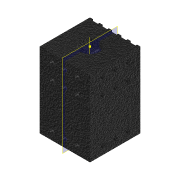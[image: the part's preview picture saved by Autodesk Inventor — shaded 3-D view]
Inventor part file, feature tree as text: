
AUTODESK INVENTOR PART (.ipt)
format: ipt  version: 2022 (Build 260153000, 153)  size: 360,448 bytes
history: native  units: mm
features: sketch x6, extrude x5, projected_geometry x3, plane x2, other x1, pattern_circular x1, pattern_linear x1, reference x1
ambient origin geometry x8: Origin, YZ Plane, XZ Plane, XY Plane, X Axis, Y Axis, Z Axis, Center Point
bodies: Volumenkörper1 (feature_tree)
feature tree (20):
  extrude  "Extrusion1"  Depth=32.0mm
  extrude  "Extrusion2"  Depth=5.0mm
  extrude  "Extrusion3"  Depth=2.8mm
  extrude  "Extrusion4"  Depth=8.0mm
  other  "Arbeitsachse1"
  pattern_circular  "Runde Anordnung1"  [2 undecoded]
  sketch  "Sketch6"  dims[d12=2.8mm]
  extrude  "Extrusion6"  Depth=8.0mm TaperAngle=0.0deg
  pattern_linear  "Rectangular Pattern1"  Spacing1=12.0mm  [1 undecoded]
  plane  "Work Plane1"
  plane  "Work Plane2"
  sketch  "Skizze1"  dims[d0=32.0mm d1=32.0mm]
  sketch  "Skizze2"  dims[d2=48.0mm d3=0.0mm d4=5.0mm]
  projected_geometry  "Projizierte Kontur1"
  sketch  "Skizze3"  dims[d5=2.8mm d8=2.8mm]
  sketch  "Skizze4"  dims[d10=8.0mm d11=2.8mm]
  reference  "Referenz1"
  projected_geometry  "Projizierte Kontur2"
  sketch  "Sketch7"  dims[d13=8.0mm d14=0.0mm d15=5.0mm d16=8.0mm d17=0.0mm d18=12.0mm d19=5.0mm d20=0.0mm d23=10.0mm d28=40.0mm d29=360.0deg d40=8.0mm d41=8.0mm d42=8.0mm d43=8.0mm d44=2.8mm d45=2.8mm d46=2.8mm d47=2.8mm d48=2.0mm d49=2.0mm d50=1.0mm d51=0.0mm d52=30.0mm d54=6.0mm d55=30.0mm d57=6.0mm]
  projected_geometry  "Projected Loop3"
note: 3 required parameter values undecoded (feature->parameter linkage not recoverable at this tier; creation-order binding heuristic only, values carry confidence <= 0.55)
